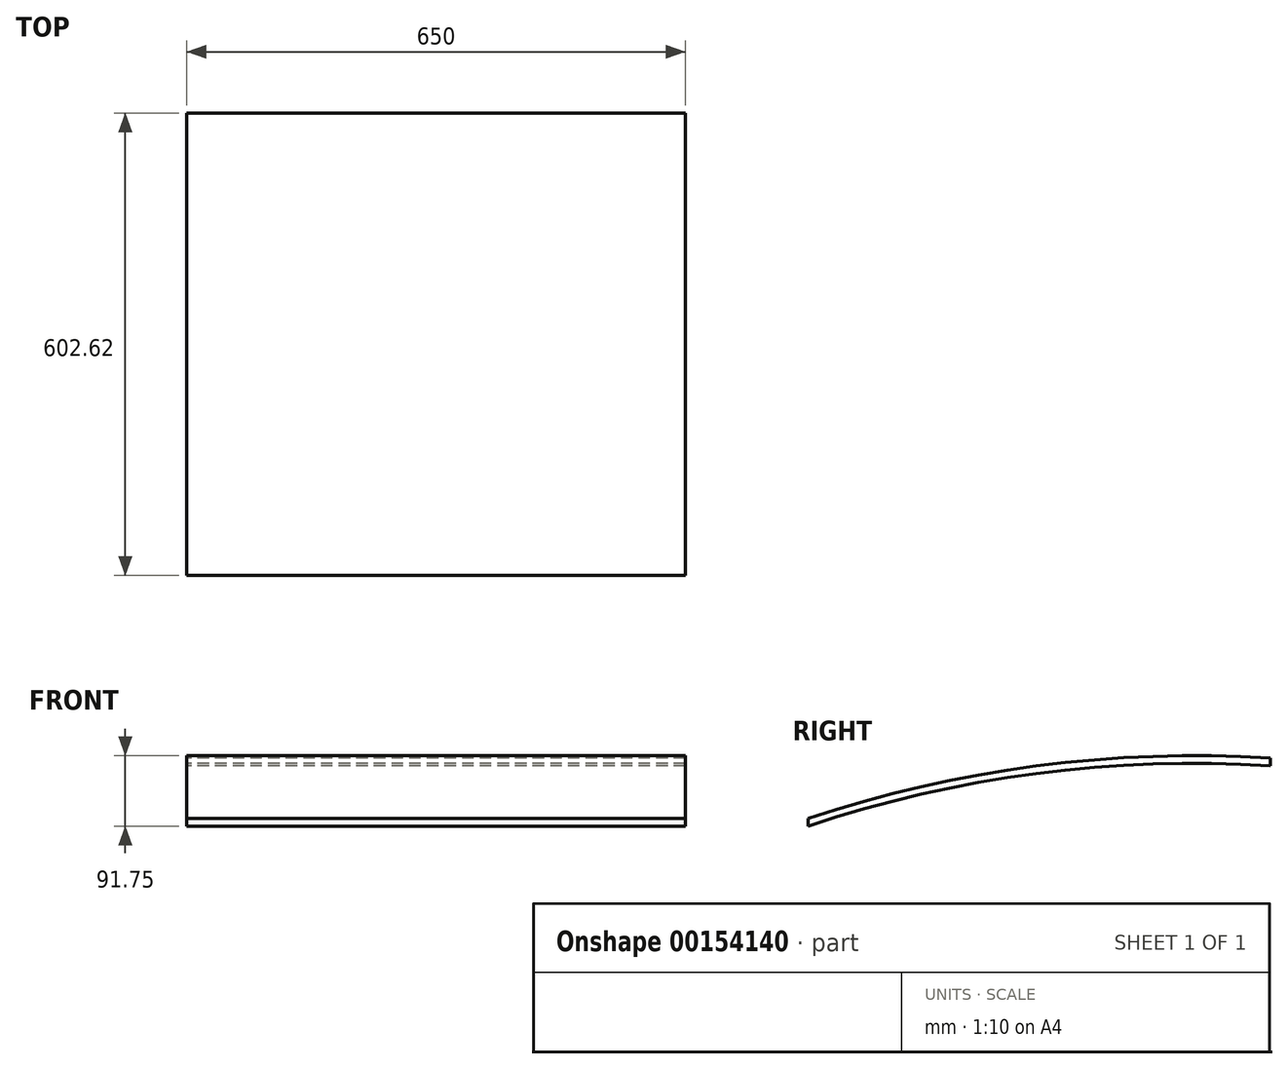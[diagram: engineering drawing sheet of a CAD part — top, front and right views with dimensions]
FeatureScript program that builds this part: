
annotation { "Feature Type Name" : "Feature", "Feature Type Description" : "" }
export const myFeature = defineFeature(function(context is Context, id is Id, definition is map)
    precondition{}
    {
        {
            var Q0;
            Q0=qCreatedBy(makeId("Right.planeOp"),FACE);
            var sketch = newSketch(context, id + "F0", { "sketchPlane" : qUnion([Q0])});
            skArc(sketch, "E0", {"start": v(141.6, 25.37) * mm, "mid": v(-163.48, 14.81) * mm, "end": v(-461.02, -53.42) * mm});
            skLineSegment(sketch, "E1", {"start": v(-461.02, -53.42) * mm, "end": v(-461.02, -63.42) * mm});
            skLineSegment(sketch, "E2", {"start": v(141.6, 25.37) * mm, "end": v(141.6, 15.37) * mm});
            skArc(sketch, "E3", {"start": v(141.6, 15.37) * mm, "mid": v(-163.51, 5.04) * mm, "end": v(-461.02, -63.42) * mm});
            skSolve(sketch);
        }
        {
            var Q0;
            Q0 = qSketchRegion(id + "F0", true);
            extrude(context, id + "F1", {"entities" : qUnion([Q0]), "endBound" : BoundingType.SYMMETRIC, "depth" : 650 * mm});
        }
    });
